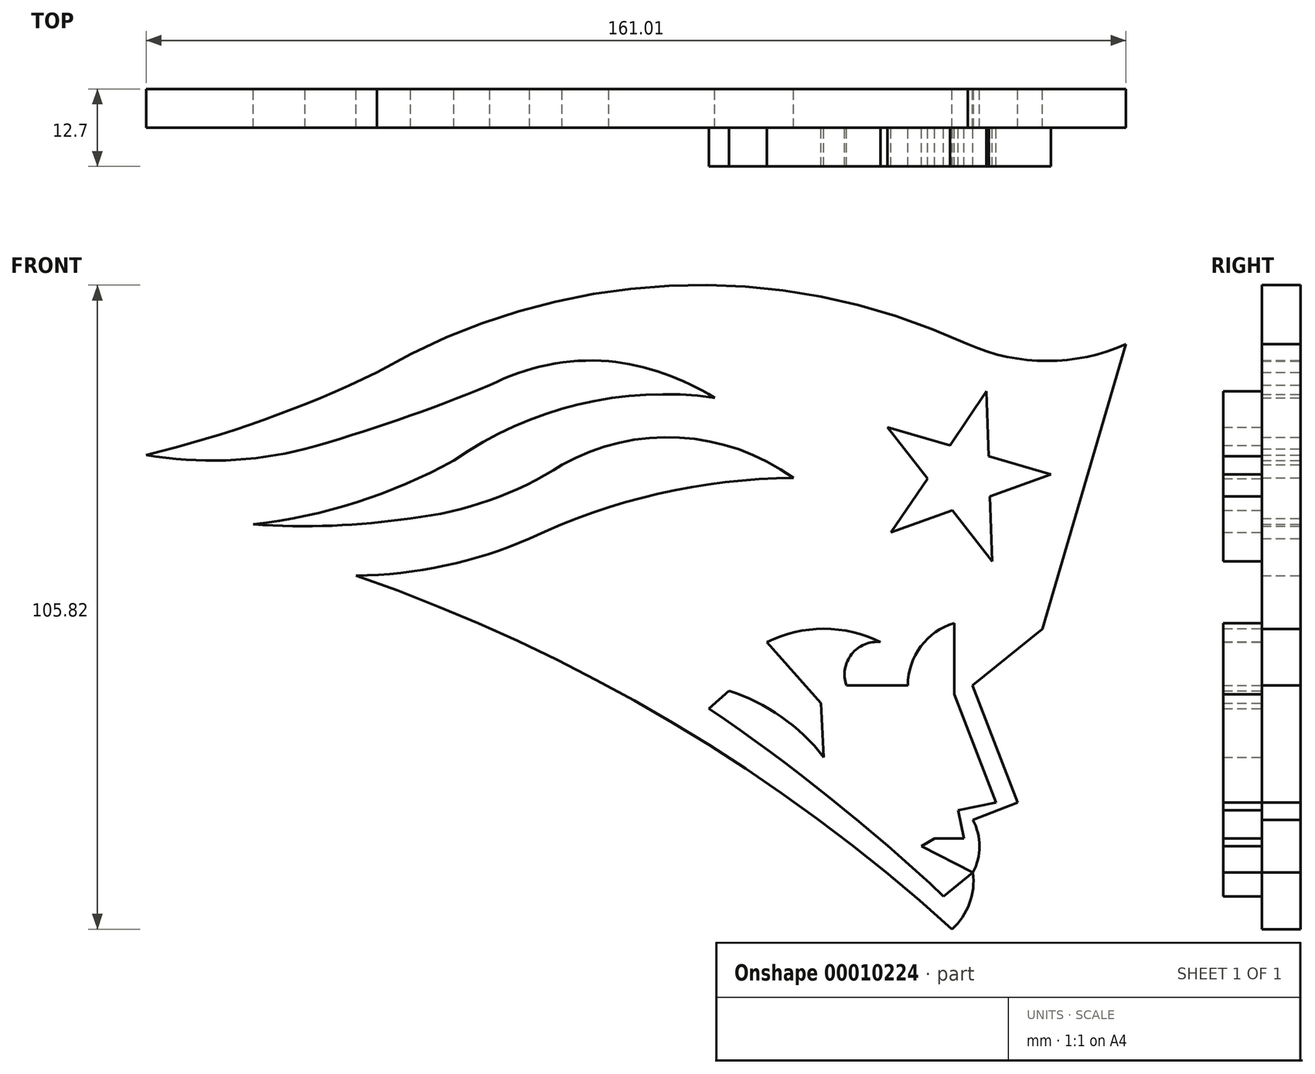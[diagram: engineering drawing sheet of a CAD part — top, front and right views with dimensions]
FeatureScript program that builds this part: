
annotation { "Feature Type Name" : "Feature", "Feature Type Description" : "" }
export const myFeature = defineFeature(function(context is Context, id is Id, definition is map)
    precondition{}
    {
        {
            var Q0;
            Q0=qCreatedBy(makeId("Front.planeOp"),FACE);
            var sketch = newSketch(context, id + "F0", { "sketchPlane" : qUnion([Q0])});
            skLineSegment(sketch, "E0", {"start": v(29.54, 58.43) * mm, "end": v(15.81, 11.69) * mm});
            skLineSegment(sketch, "E1", {"start": v(15.81, 11.69) * mm, "end": v(4.31, 2.41) * mm});
            skLineSegment(sketch, "E2", {"start": v(4.31, 2.41) * mm, "end": v(11.73, -16.88) * mm});
            skLineSegment(sketch, "E3", {"start": v(11.73, -16.88) * mm, "end": v(4.4, -19.7) * mm});
            skArc(sketch, "E4", {"start": v(4.4, -28.38) * mm, "mid": v(5.44, -24.04) * mm, "end": v(4.4, -19.7) * mm});
            skArc(sketch, "E5", {"start": v(0.97, -37.66) * mm, "mid": v(3.82, -33.44) * mm, "end": v(4.4, -28.38) * mm});
            skArc(sketch, "E6", {"start": v(3.57, 58.43) * mm, "mid": v(16.55, 55.7) * mm, "end": v(29.54, 58.43) * mm});
            skLineSegment(sketch, "E7", {"start": v(3.57, 58.43) * mm, "end": v(3.57, 58.43) * mm});
            skArc(sketch, "E8", {"start": v(-88, 29.84) * mm, "mid": v(-75.04, 32.8) * mm, "end": v(-63.12, 38.63) * mm});
            skArc(sketch, "E9", {"start": v(-113.86, 28.84) * mm, "mid": v(-100.9, 28.64) * mm, "end": v(-88, 29.84) * mm});
            skArc(sketch, "E10", {"start": v(-113.86, 28.84) * mm, "mid": v(-96.86, 32.47) * mm, "end": v(-80.88, 39.33) * mm});
            skArc(sketch, "E11", {"start": v(-38.05, 49.66) * mm, "mid": v(-60.44, 48.54) * mm, "end": v(-80.88, 39.33) * mm});
            skArc(sketch, "E12", {"start": v(-25.1, 36.46) * mm, "mid": v(-43.8, 43.1) * mm, "end": v(-63.12, 38.63) * mm});
            skArc(sketch, "E13", {"start": v(-131.47, 40.25) * mm, "mid": v(-112.15, 46) * mm, "end": v(-93.55, 53.8) * mm});
            skArc(sketch, "E14", {"start": v(3.57, 58.43) * mm, "mid": v(-45.56, 68.04) * mm, "end": v(-93.55, 53.8) * mm});
            skArc(sketch, "E15", {"start": v(-131.47, 40.25) * mm, "mid": v(-118.36, 39.37) * mm, "end": v(-105.35, 41.23) * mm});
            skArc(sketch, "E16", {"start": v(-38.05, 49.66) * mm, "mid": v(-46.42, 53.62) * mm, "end": v(-55.45, 55.66) * mm});
            skPoint(sketch, "E17.visualSharp", {"position": v(-67.17, 55.3) * mm});
            skArc(sketch, "E17.filletArc", {"start": v(-66.32, 55.44) * mm, "mid": v(-67.12, 55.26) * mm, "end": v(-67.9, 54.97) * mm});
            skArc(sketch, "E18", {"start": v(-105.35, 41.23) * mm, "mid": v(-90.02, 46.03) * mm, "end": v(-75, 51.7) * mm});
            skArc(sketch, "E19", {"start": v(-96.94, 20.41) * mm, "mid": v(-82.4, 22.04) * mm, "end": v(-68.47, 26.51) * mm});
            skArc(sketch, "E20", {"start": v(-25.1, 36.46) * mm, "mid": v(-47.33, 33.86) * mm, "end": v(-68.47, 26.51) * mm});
            skArc(sketch, "E21", {"start": v(0.97, -37.66) * mm, "mid": v(-45.06, -3.69) * mm, "end": v(-96.94, 20.41) * mm});
            skArc(sketch, "E22", {"start": v(-55.45, 55.66) * mm, "mid": v(-65.5, 55.04) * mm, "end": v(-75, 51.7) * mm});
            skSolve(sketch);
        }
        {
            var Q0;
            Q0=makeQuery(id+"F0.imprint","IMPRINT",FACE,{"disambiguationData":[TD([[makeQuery(id+"F0.imprint","IMPRINT",EDGE,{"derivedFrom":sQuery(id+"F0.wireOp",EDGE,"E0")}),-1.0]])]});
            extrude(context, id + "F1", {"entities" : qUnion([Q0]), "depth" : 6.35 * mm});
        }
        {
            var Q0;
            Q0=makeQuery(id+"F1.opExtrude","CAP_FACE",FACE,{"disambiguationData":[OSD([sQuery(id+"F0.wireOp",EDGE,"E0"),sQuery(id+"F0.wireOp",EDGE,"E1"),sQuery(id+"F0.wireOp",EDGE,"E2"),sQuery(id+"F0.wireOp",EDGE,"E3"),sQuery(id+"F0.wireOp",EDGE,"E4"),sQuery(id+"F0.wireOp",EDGE,"E5"),sQuery(id+"F0.wireOp",EDGE,"E6"),sQuery(id+"F0.wireOp",EDGE,"5a7b0ea9-7add-4295-b359-09b799b26604"),sQuery(id+"F0.wireOp",EDGE,"a772a3d0-a05f-469f-ac4a-95de44ba73e0"),sQuery(id+"F0.wireOp",EDGE,"E7"),sQuery(id+"F0.wireOp",EDGE,"4a6b9d04-7878-4ad2-be5b-53405a07bcb8"),sQuery(id+"F0.wireOp",EDGE,"174b4cb9-bad4-48d5-bccc-986990c096a6"),sQuery(id+"F0.wireOp",EDGE,"bac64411-df81-4d94-83e7-b5dda78b5204"),sQuery(id+"F0.wireOp",EDGE,"cdebb211-51cd-4c1b-a1cf-e8e0b51789ba")])],"isStart":false});
            var sketch = newSketch(context, id + "F2", { "sketchPlane" : qUnion([Q0])});
            skArc(sketch, "E23", {"start": v(1.33, 12.6) * mm, "mid": v(-4.19, 8.78) * mm, "end": v(-6.3, 2.41) * mm});
            skLineSegment(sketch, "E24", {"start": v(-6.3, 2.41) * mm, "end": v(-16.42, 2.41) * mm});
            skArc(sketch, "E25", {"start": v(-10.79, 9.52) * mm, "mid": v(-15.54, 7.5) * mm, "end": v(-16.42, 2.41) * mm});
            skArc(sketch, "E26", {"start": v(-10.79, 9.52) * mm, "mid": v(-20.12, 11.7) * mm, "end": v(-29.45, 9.52) * mm});
            skLineSegment(sketch, "E27", {"start": v(-29.45, 9.52) * mm, "end": v(-20.57, -0.56) * mm});
            skLineSegment(sketch, "E28", {"start": v(-20.57, -0.56) * mm, "end": v(-20.12, -9.4) * mm});
            skArc(sketch, "E29", {"start": v(-20.12, -9.4) * mm, "mid": v(-27.09, -2.78) * mm, "end": v(-35.68, 1.52) * mm});
            skLineSegment(sketch, "E30", {"start": v(-35.68, 1.52) * mm, "end": v(-38.98, -1.4) * mm});
            skArc(sketch, "E31", {"start": v(-0.42, -32.26) * mm, "mid": v(-19.11, -16.1) * mm, "end": v(-38.98, -1.4) * mm});
            skLineSegment(sketch, "E32", {"start": v(8.17, -16.88) * mm, "end": v(1.97, -18.12) * mm});
            skLineSegment(sketch, "E33", {"start": v(1.97, -18.12) * mm, "end": v(2.9, -22.77) * mm});
            skLineSegment(sketch, "E34", {"start": v(2.9, -22.77) * mm, "end": v(-1.9, -22.77) * mm});
            skLineSegment(sketch, "E35", {"start": v(-1.9, -22.77) * mm, "end": v(-4.07, -24.04) * mm});
            skLineSegment(sketch, "E36", {"start": v(-4.07, -24.04) * mm, "end": v(4.4, -28.38) * mm});
            skLineSegment(sketch, "E37", {"start": v(4.4, -28.38) * mm, "end": v(-0.42, -32.26) * mm});
            skLineSegment(sketch, "E38", {"start": v(8.17, -16.88) * mm, "end": v(1.33, 0.9) * mm});
            skLineSegment(sketch, "E39", {"start": v(1.33, 0.9) * mm, "end": v(1.33, 12.6) * mm});
            skCircle(sketch, "E40.cCircle", {"center": v(2.54, 36.56) * mm, "radius": 4.54 * mm, "construction": true});
            skLineSegment(sketch, "E40.0", {"start": v(-3.07, 36.38) * mm, "end": v(0.63, 41.85) * mm});
            skLineSegment(sketch, "E40.1", {"start": v(0.63, 41.85) * mm, "end": v(6.97, 40.02) * mm});
            skLineSegment(sketch, "E40.2", {"start": v(6.97, 40.02) * mm, "end": v(7.2, 33.42) * mm});
            skLineSegment(sketch, "E40.3", {"start": v(7.2, 33.42) * mm, "end": v(0.98, 31.17) * mm});
            skLineSegment(sketch, "E40.4", {"start": v(0.98, 31.17) * mm, "end": v(-3.07, 36.38) * mm});
            skPoint(sketch, "E40.0.midPoint", {"position": v(-1.22, 39.11) * mm});
            skLineSegment(sketch, "E41", {"start": v(7.2, 33.42) * mm, "end": v(7.55, 22.74) * mm});
            skLineSegment(sketch, "E42", {"start": v(7.55, 22.74) * mm, "end": v(0.98, 31.17) * mm});
            skLineSegment(sketch, "E43", {"start": v(0.98, 31.17) * mm, "end": v(-9.06, 27.53) * mm});
            skLineSegment(sketch, "E44", {"start": v(-9.06, 27.53) * mm, "end": v(-3.07, 36.38) * mm});
            skLineSegment(sketch, "E45", {"start": v(-3.07, 36.38) * mm, "end": v(-9.64, 44.8) * mm});
            skLineSegment(sketch, "E46", {"start": v(-9.64, 44.8) * mm, "end": v(0.63, 41.85) * mm});
            skLineSegment(sketch, "E47", {"start": v(6.97, 40.02) * mm, "end": v(17.23, 37.06) * mm});
            skLineSegment(sketch, "E48", {"start": v(17.23, 37.06) * mm, "end": v(7.2, 33.42) * mm});
            skLineSegment(sketch, "E49", {"start": v(6.97, 40.02) * mm, "end": v(6.61, 50.7) * mm});
            skLineSegment(sketch, "E50", {"start": v(6.61, 50.7) * mm, "end": v(0.63, 41.85) * mm});
            skSolve(sketch);
        }
        {
            var Q0;
            Q0=makeQuery(id+"F2.imprint","IMPRINT",FACE,{"disambiguationData":[TD([[makeQuery(id+"F2.imprint","IMPRINT",EDGE,{"derivedFrom":sQuery(id+"F2.wireOp",EDGE,"f87b9d5e-e48a-4e62-b66d-5e8aaa541502")}),-1.0]])]});
            var Q1;
            Q1=makeQuery(id+"F2.imprint","IMPRINT",FACE,{"disambiguationData":[TD([[makeQuery(id+"F2.imprint","IMPRINT",EDGE,{"derivedFrom":sQuery(id+"F2.wireOp",EDGE,"E23")}),1.0]])]});
            extrude(context, id + "F3", {"entities" : qUnion([Q0, Q1]), "operationType" : NewBodyOperationType.ADD, "depth" : 6.35 * mm});
        }
        {
            var Q0;
            Q0=qSketchRegion(id+"F2",true);
            extrude(context, id + "F4", {"entities" : qUnion([Q0]), "operationType" : NewBodyOperationType.ADD, "depth" : 6.35 * mm});
        }
    });
